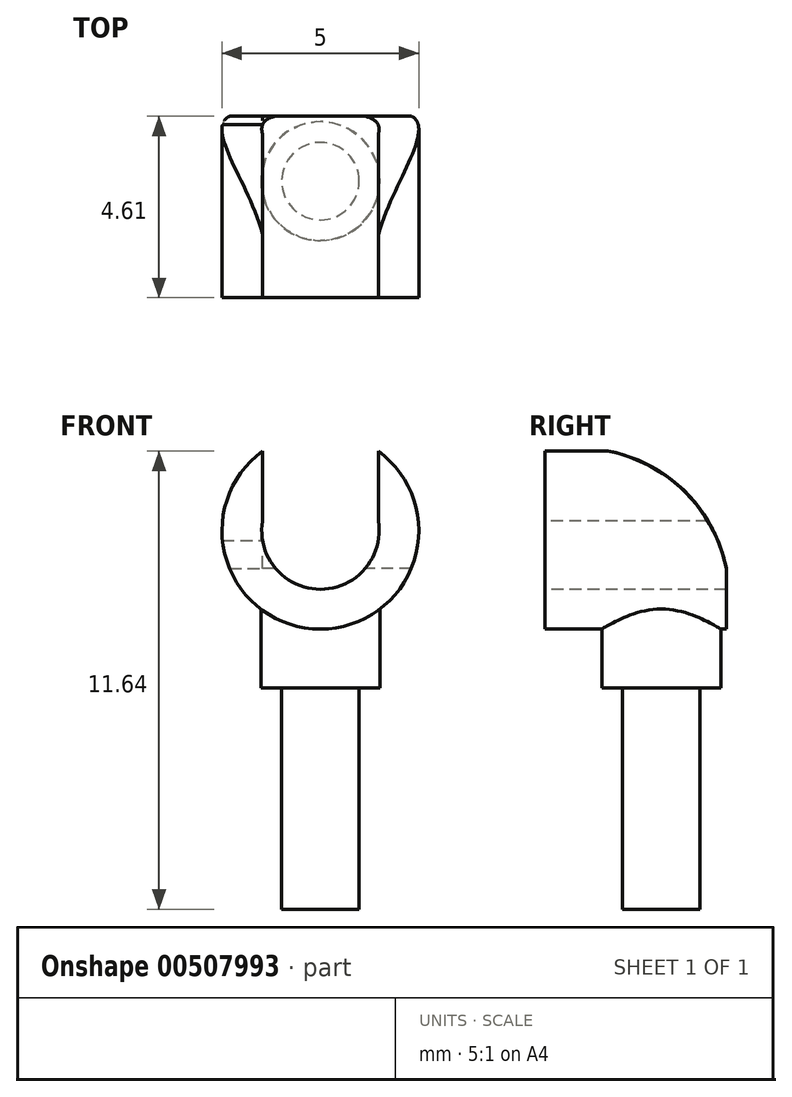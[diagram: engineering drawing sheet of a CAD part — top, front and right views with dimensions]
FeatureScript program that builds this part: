
annotation { "Feature Type Name" : "Feature", "Feature Type Description" : "" }
export const myFeature = defineFeature(function(context is Context, id is Id, definition is map)
    precondition{}
    {
        {
            var Q0;
            Q0=qCreatedBy(makeId("Front.planeOp"),FACE);
            var sketch = newSketch(context, id + "F0", { "sketchPlane" : qUnion([Q0])});
            skCircle(sketch, "E0", {"center": v(0, 0) * mm, "radius": 2.5 * mm});
            skSolve(sketch);
        }
        {
            var Q0;
            Q0 = qSketchRegion(id + "F0", true);
            extrude(context, id + "F1", {"entities" : qUnion([Q0]), "depth" : 4.61 * mm, "offsetDistance" : 25 * mm});
        }
        {
            var Q0;
            Q0=makeQuery(id+"F1.opExtrude","CAP_FACE",FACE,{"disambiguationData":[OSD([sQuery(id+"F0.wireOp",EDGE,"E0")])],"isStart":false});
            var sketch = newSketch(context, id + "F2", { "sketchPlane" : qUnion([Q0])});
            skCircle(sketch, "E1", {"center": v(0, 0) * mm, "radius": 1.49 * mm});
            skSolve(sketch);
        }
        {
            var Q0;
            Q0 = qSketchRegion(id + "F2", true);
            extrude(context, id + "F3", {"entities" : qUnion([Q0]), "operationType" : NewBodyOperationType.REMOVE, "oppositeDirection" : true, "depth" : 400 * mm, "offsetDistance" : 25 * mm});
        }
        {
            var Q0;
            Q0=makeQuery(id+"F1.opExtrude","CAP_FACE",FACE,{"disambiguationData":[OSD([sQuery(id+"F0.wireOp",EDGE,"E0")])],"isStart":false});
            var sketch = newSketch(context, id + "F4", { "sketchPlane" : qUnion([Q0])});
            skLineSegment(sketch, "E2", {"start": v(-1.47, 2.02) * mm, "end": v(-1.47, 0.24) * mm});
            skLineSegment(sketch, "E3", {"start": v(-1.47, 0.24) * mm, "end": v(1.47, 0.24) * mm});
            skLineSegment(sketch, "E4", {"start": v(1.47, 0.24) * mm, "end": v(1.47, 2.02) * mm});
            skArc(sketch, "E5", {"start": v(1.47, 2.02) * mm, "mid": v(0, 2.64) * mm, "end": v(-1.47, 2.02) * mm});
            skSolve(sketch);
        }
        {
            var Q0;
            {var subQ0=sQuery(id+"F4.wireOp",EDGE,"E5");Q0=makeQuery(id+"F4.imprint","IMPRINT",FACE,{"disambiguationData":[TD([[makeQuery(id+"F4.imprint","IMPRINT",EDGE,{"derivedFrom":subQ0}),1.0]])]});}
            var Q1;
            {var subQ0=sQuery(id+"F4.wireOp",EDGE,"E3");Q1=makeQuery(id+"F4.imprint","IMPRINT",FACE,{"disambiguationData":[TD([[makeQuery(id+"F4.imprint","IMPRINT",EDGE,{"derivedFrom":subQ0}),1.0]])]});}
            var Q2;
            {var subQ0=sQuery(id+"F4.wireOp",EDGE,"E2");Q2=makeQuery(id+"F4.imprint","IMPRINT",FACE,{"disambiguationData":[TD([[makeQuery(id+"F4.imprint","IMPRINT",EDGE,{"derivedFrom":subQ0}),1.0]])]});}
            extrude(context, id + "F5", {"entities" : qUnion([Q0, Q1, Q2]), "operationType" : NewBodyOperationType.REMOVE, "oppositeDirection" : true, "depth" : 25 * mm, "offsetDistance" : 25 * mm});
        }
        {
            var Q0;
            Q0=qCreatedBy(makeId("Top.planeOp"),FACE);
            var sketch = newSketch(context, id + "F6", { "sketchPlane" : qUnion([Q0])});
            skCircle(sketch, "E6", {"center": v(0, -1.65) * mm, "radius": 1.51 * mm});
            skSolve(sketch);
        }
        {
            var Q0;
            Q0 = qSketchRegion(id + "F6", true);
            extrude(context, id + "F7", {"entities" : qUnion([Q0]), "operationType" : NewBodyOperationType.ADD, "oppositeDirection" : true, "depth" : 5.1 * mm, "offsetDistance" : 25 * mm});
        }
        {
            var Q0;
            Q0=makeQuery(id+"F1.opExtrude","CAP_FACE",FACE,{"disambiguationData":[OSD([sQuery(id+"F0.wireOp",EDGE,"E0")])],"isStart":false});
            var sketch = newSketch(context, id + "F8", { "sketchPlane" : qUnion([Q0])});
            skArc(sketch, "E7", {"start": v(-1.49, 0) * mm, "mid": v(0, -1.49) * mm, "end": v(1.49, 0) * mm});
            skLineSegment(sketch, "E8", {"start": v(-1.5, 0) * mm, "end": v(0.34, 0.72) * mm});
            skLineSegment(sketch, "E9", {"start": v(0.34, 0.72) * mm, "end": v(1.49, 0) * mm});
            skSolve(sketch);
        }
        {
            var Q0;
            Q0 = qSketchRegion(id + "F8", true);
            extrude(context, id + "F9", {"entities" : qUnion([Q0]), "operationType" : NewBodyOperationType.REMOVE, "oppositeDirection" : true, "depth" : 25 * mm, "offsetDistance" : 25 * mm});
        }
        {
            var Q0;
            Q0=makeQuery(id+"F1.opExtrude","CAP_FACE",FACE,{"disambiguationData":[OSD([sQuery(id+"F0.wireOp",EDGE,"E0")])],"isStart":false});
            var sketch = newSketch(context, id + "F10", { "sketchPlane" : qUnion([Q0])});
            skLineSegment(sketch, "E10", {"start": v(-3.07, -4) * mm, "end": v(3.3, -4) * mm});
            skLineSegment(sketch, "E11", {"start": v(-3.07, -4) * mm, "end": v(-2.94, -5.35) * mm});
            skLineSegment(sketch, "E12", {"start": v(-2.94, -5.35) * mm, "end": v(2.52, -5.28) * mm});
            skLineSegment(sketch, "E13", {"start": v(2.52, -5.28) * mm, "end": v(3.3, -4) * mm});
            skSolve(sketch);
        }
        {
            var Q0;
            Q0 = qSketchRegion(id + "F10", true);
            extrude(context, id + "F11", {"entities" : qUnion([Q0]), "operationType" : NewBodyOperationType.REMOVE, "oppositeDirection" : true, "depth" : 25 * mm, "offsetDistance" : 25 * mm});
        }
        {
            var Q0;
            Q0=qCreatedBy(makeId("Right.planeOp"),FACE);
            var sketch = newSketch(context, id + "F12", { "sketchPlane" : qUnion([Q0])});
            skArc(sketch, "E14", {"start": v(0, -2.5) * mm, "mid": v(-0.59, 0.43) * mm, "end": v(-3.1, 2.04) * mm});
            skLineSegment(sketch, "E15", {"start": v(0, -2.5) * mm, "end": v(1.42, 3) * mm});
            skLineSegment(sketch, "E16", {"start": v(1.42, 3) * mm, "end": v(-2.94, 3.13) * mm});
            skLineSegment(sketch, "E17", {"start": v(-2.94, 3.13) * mm, "end": v(-3.1, 2.04) * mm});
            skSolve(sketch);
        }
        {
            var Q0;
            Q0 = qSketchRegion(id + "F12", true);
            extrude(context, id + "F13", {"entities" : qUnion([Q0]), "operationType" : NewBodyOperationType.REMOVE, "endBound" : BoundingType.THROUGH_ALL, "depth" : 25 * mm, "offsetDistance" : 25 * mm});
        }
        {
            var Q0;
            Q0=makeQuery(id+"F5.boolean.opBoolean","COPY",FACE,{"derivedFrom":makeQuery(id+"F5.opExtrude","SWEPT_FACE",FACE,{"disambiguationData":[OSD([sQuery(id+"F4.wireOp",EDGE,"E2")])]})});
            var sketch = newSketch(context, id + "F14", { "sketchPlane" : qUnion([Q0])});
            skArc(sketch, "E18", {"start": v(0, -0.96) * mm, "mid": v(-1.04, 1) * mm, "end": v(-3, 2.02) * mm});
            skLineSegment(sketch, "E19", {"start": v(-3, 2.02) * mm, "end": v(0.18, 2.2) * mm});
            skLineSegment(sketch, "E20", {"start": v(0.18, 2.2) * mm, "end": v(0.18, -0.2) * mm});
            skLineSegment(sketch, "E21", {"start": v(0.18, -0.2) * mm, "end": v(0, -0.96) * mm});
            skSolve(sketch);
        }
        {
            var Q0;
            Q0 = qSketchRegion(id + "F14", true);
            extrude(context, id + "F15", {"entities" : qUnion([Q0]), "operationType" : NewBodyOperationType.REMOVE, "oppositeDirection" : true, "depth" : 25 * mm, "offsetDistance" : 25 * mm});
        }
        {
            var Q0;
            Q0=qCreatedBy(makeId("Right.planeOp"),FACE);
            var sketch = newSketch(context, id + "F16", { "sketchPlane" : qUnion([Q0])});
            skArc(sketch, "E22", {"start": v(0, -0.94) * mm, "mid": v(-0.1, -0.59) * mm, "end": v(-0.22, -0.24) * mm});
            skLineSegment(sketch, "E23", {"start": v(-0.22, -0.24) * mm, "end": v(0, -0.08) * mm});
            skLineSegment(sketch, "E24", {"start": v(0, -0.08) * mm, "end": v(0.19, -0.42) * mm});
            skLineSegment(sketch, "E25", {"start": v(0.19, -0.42) * mm, "end": v(0, -0.94) * mm});
            skSolve(sketch);
        }
        {
            var Q0;
            Q0 = qSketchRegion(id + "F16", true);
            extrude(context, id + "F17", {"entities" : qUnion([Q0]), "operationType" : NewBodyOperationType.REMOVE, "oppositeDirection" : true, "depth" : 25 * mm, "offsetDistance" : 25 * mm});
        }
        {
            var Q0;
            Q0=makeQuery(id+"F11.boolean.opBoolean","COPY",FACE,{"derivedFrom":makeQuery(id+"F11.opExtrude","SWEPT_FACE",FACE,{"disambiguationData":[OSD([sQuery(id+"F10.wireOp",EDGE,"E10")])]})});
            var sketch = newSketch(context, id + "F18", { "sketchPlane" : qUnion([Q0])});
            skCircle(sketch, "E26", {"center": v(0, 1.65) * mm, "radius": 0.98 * mm});
            skSolve(sketch);
        }
        {
            var Q0;
            Q0 = qSketchRegion(id + "F18", true);
            extrude(context, id + "F19", {"entities" : qUnion([Q0]), "operationType" : NewBodyOperationType.ADD, "depth" : 5.62 * mm, "offsetDistance" : 25 * mm});
        }
    });
